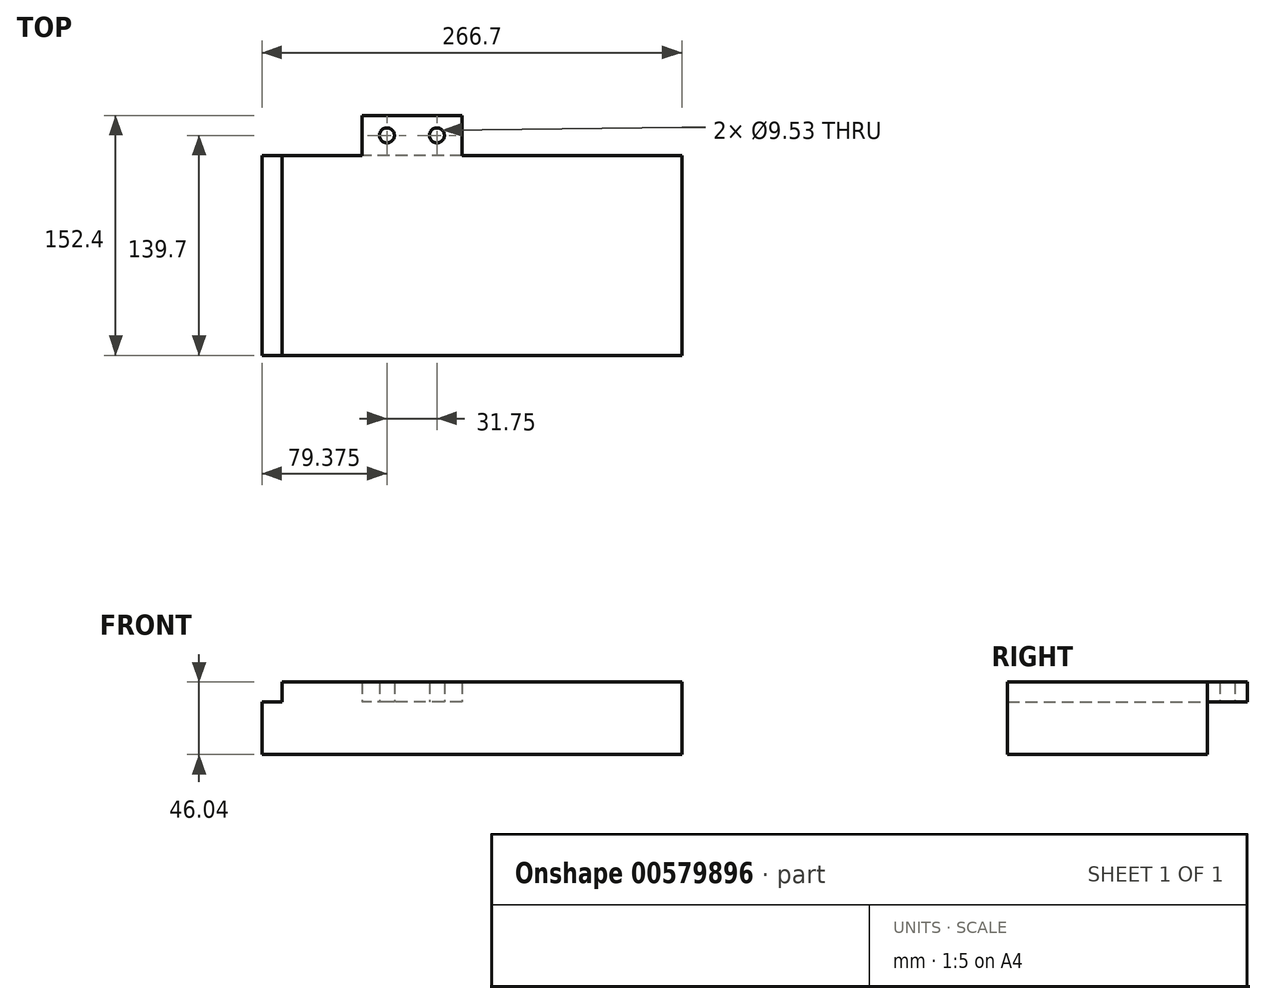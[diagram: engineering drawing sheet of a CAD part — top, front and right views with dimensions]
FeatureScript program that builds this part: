
annotation { "Feature Type Name" : "Feature", "Feature Type Description" : "" }
export const myFeature = defineFeature(function(context is Context, id is Id, definition is map)
    precondition{}
    {
        {
            var Q0;
            Q0=qCreatedBy(makeId("Top.planeOp"),FACE);
            var sketch = newSketch(context, id + "F0", { "sketchPlane" : qUnion([Q0])});
            skLineSegment(sketch, "E0.bottom", {"start": v(0, 0) * mm, "end": v(-266.7, 0) * mm});
            skLineSegment(sketch, "E0.top", {"start": v(0, 127) * mm, "end": v(-266.7, 127) * mm});
            skLineSegment(sketch, "E0.left", {"start": v(0, 0) * mm, "end": v(0, 127) * mm});
            skLineSegment(sketch, "E0.right", {"start": v(-266.7, 0) * mm, "end": v(-266.7, 127) * mm});
            skSolve(sketch);
        }
        {
            var Q0;
            Q0 = qSketchRegion(id + "F0", true);
            extrude(context, id + "F1", {"entities" : qUnion([Q0]), "depth" : 33.34 * mm, "offsetDistance" : 25.4 * mm});
        }
        {
            var Q0;
            Q0=makeQuery(id+"F1.opExtrude","CAP_FACE",FACE,{"disambiguationData":[OSD([sQuery(id+"F0.wireOp",EDGE,"E0.bottom"),sQuery(id+"F0.wireOp",EDGE,"E0.top"),sQuery(id+"F0.wireOp",EDGE,"E0.left"),sQuery(id+"F0.wireOp",EDGE,"E0.right")])],"isStart":false});
            var sketch = newSketch(context, id + "F2", { "sketchPlane" : qUnion([Q0])});
            skLineSegment(sketch, "E1.bottom", {"start": v(0, 0) * mm, "end": v(-254, 0) * mm});
            skLineSegment(sketch, "E1.top", {"start": v(0, 127) * mm, "end": v(-254, 127) * mm});
            skLineSegment(sketch, "E1.left", {"start": v(0, 0) * mm, "end": v(0, 127) * mm});
            skLineSegment(sketch, "E1.right", {"start": v(-254, 0) * mm, "end": v(-254, 127) * mm});
            skLineSegment(sketch, "E2.bottom", {"start": v(-203.2, 127) * mm, "end": v(-139.7, 127) * mm});
            skLineSegment(sketch, "E2.top", {"start": v(-203.2, 152.4) * mm, "end": v(-139.7, 152.4) * mm});
            skLineSegment(sketch, "E2.left", {"start": v(-203.2, 127) * mm, "end": v(-203.2, 152.4) * mm});
            skLineSegment(sketch, "E2.right", {"start": v(-139.7, 127) * mm, "end": v(-139.7, 152.4) * mm});
            skCircle(sketch, "E3", {"center": v(-187.32, 139.7) * mm, "radius": 4.76 * mm});
            skPoint(sketch, "E3.centerSnap0", {"position": v(-203.2, 139.7) * mm});
            skCircle(sketch, "E4", {"center": v(-155.57, 139.7) * mm, "radius": 4.76 * mm});
            skPoint(sketch, "E4.centerSnap0", {"position": v(-139.7, 139.7) * mm});
            skSolve(sketch);
        }
        {
            var Q0;
            Q0 = qSketchRegion(id + "F2", true);
            extrude(context, id + "F3", {"entities" : qUnion([Q0]), "operationType" : NewBodyOperationType.ADD, "depth" : 12.7 * mm, "offsetDistance" : 25.4 * mm});
        }
    });
